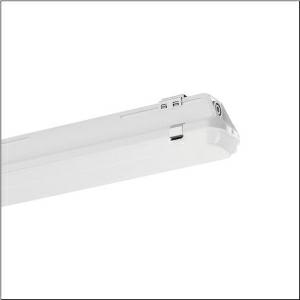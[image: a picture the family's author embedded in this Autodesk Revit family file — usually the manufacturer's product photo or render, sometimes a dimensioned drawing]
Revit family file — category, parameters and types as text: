
# Revit family: monsun_r__21_51fb107p460c_c7f7
name_source: partatom
category: Lighting Fixtures
units: mm (PartAtom-declared; Revit-internal decimal feet)

## family parameters
Cut with Voids When Loaded = No
Host = Face
Light Source = No
Part Type = Normal
Room Calculation Point = No
Round Connector Dimension = Use Diameter
Shared = No

## types (1)
- Monsun® 21 (1 x LED, 6200 lm, 34.9 W, 4000K)
    Apparent Load = 35 VA
    CIE Flux Codes = 47 77 93 94 100
    Color Rendering = 80
    Color Temperature = 4000K
    Default Elevation = 1800 mm
    Description = Monsun® 21, damp-proof luminaire, chain hanger, primary optical cover: enclosure, of PMMA, light emission: direct distribution, primary light characteristic: symmetric, installation type: suspended mounting, surface-mounted, horizontal mounting, vertical mounting, LED, rated luminous flux: 6.200lm, luminous efficacy: 178lm/W, light colour: 840, colour temperature: 4000K, control gear: ON/OFF, with terminal, 3-pole, max. 2.5mm², mains connection: 220..240V, AC, 50/60Hz, rated input power: 35W, housing, of glass-fibre reinforced polyester, uncoated, bright grey, incl. chain hanger, length: 1.590mm, width: 90mm, height: 88mm, clip for enclosure, of stainless steel (V2A), ceiling mounting element, of stainless steel (V2A), chain hanger, of stainless steel (V2A), protection rating (complete): IP66, insulation class (complete): insulation class I (protective earthing), certification: CE, ENEC, VDE, UKCA, protection symbol: D, impact resistance: IK04, permissible operating ambient temperature: -25..+35°C, standard: EN 50419, EN 60598-2-1, corresponds to IFS (International Featured Standards) requirements for safety and quality in the food industry, for indoor or canopied outdoor use, no direct snow, no direct sun, no direct rain, LABS conformity tested according to VDMA 24364:2018-05, contact your sales advisor before using the luminaires in applications with unclear chemical exposure, large temperature fluctuations or condensation-forming humidity, packaging unit: 1 piece
    Height = 89 mm
    Lamp = 1 x LED
    Lamp Light Flux = 6200 lm
    Lamp Power = 34.9 W
    Lamp count = 1
    Length = 1590 mm
    Luminous efficacy = 178 lm/W
    Manufacturer = Siteco
    ModVariant = No
    Model = 51FB107P460C
    Mounting Place = Ceiling
    Mounting Type = Surface mounted
    Number of Poles = 1
    OnlyDefault = Yes
    Power Factor = 1
    Product Name = Monsun® 21
    Product group = damp-proof luminaire
    ProductGroupID = 301
    Protection Class = Protection class I
    Protection Degree = IP 66
    RLX_Detail_Level = 1
    RLX_Emergency_Light_Flux = 0 lm
    RLX_Emergency_Type = 0
    RLX_Emergency_Type_DB = No
    RlxData = <blob elided: 88605 chars, md5=7f6f92e8>
    Socket = socket
    Standby Power = 0 W
    System Light Flux = 6200 lm
    System Power = 35 W
    Type Comments = Product without accessories
    Type Image = l_1319656.jpg
    URL = http://relux.com
    VarID = ---
    Voltage = 0 V
    Weight = 0.00 kg
    Width = 90 mm

## geometry (parser evidence)
native form markers: Blend x4, Sweep x14
no freeform markers — native parametric forms only
